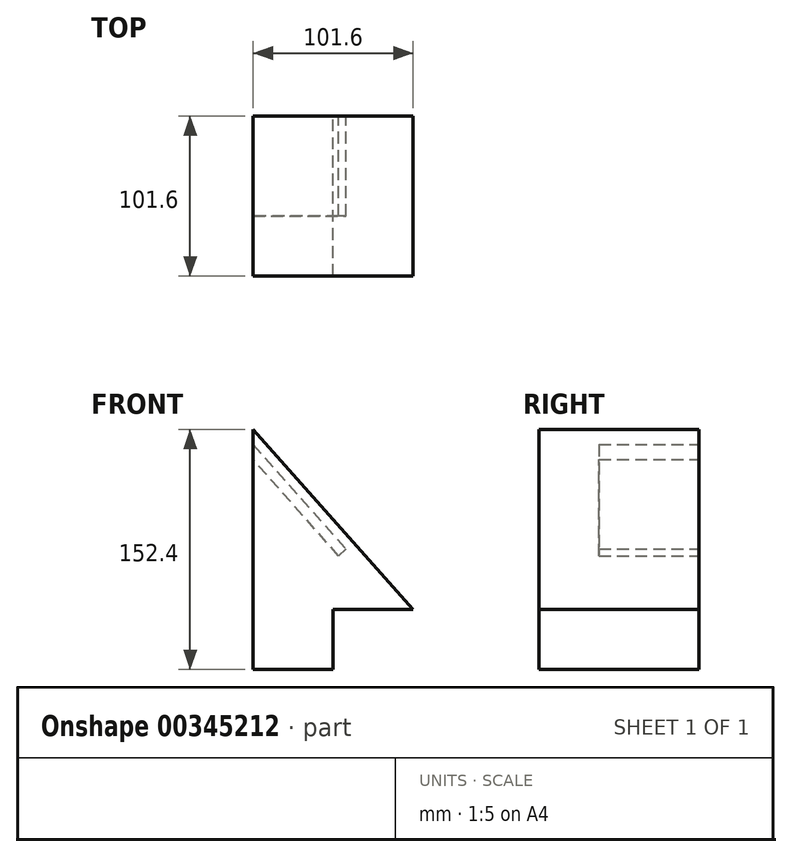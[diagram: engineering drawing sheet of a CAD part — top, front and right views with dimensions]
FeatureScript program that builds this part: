
annotation { "Feature Type Name" : "Feature", "Feature Type Description" : "" }
export const myFeature = defineFeature(function(context is Context, id is Id, definition is map)
    precondition{}
    {
        {
            var Q0;
            Q0=qCreatedBy(makeId("Front.planeOp"),FACE);
            var sketch = newSketch(context, id + "F0", { "sketchPlane" : qUnion([Q0])});
            skLineSegment(sketch, "E0.top", {"start": v(-61.33, -55.16) * mm, "end": v(-10.53, -55.16) * mm});
            skPoint(sketch, "E0.middle", {"position": v(-10.53, -36.1) * mm});
            skLineSegment(sketch, "E1", {"start": v(-10.53, -55.16) * mm, "end": v(-10.53, -17.06) * mm});
            skLineSegment(sketch, "E2", {"start": v(-10.53, -17.06) * mm, "end": v(40.27, -17.06) * mm});
            skLineSegment(sketch, "E3", {"start": v(40.27, -17.06) * mm, "end": v(-61.33, 97.24) * mm});
            skPoint(sketch, "E4.orphan", {"position": v(40.27, -55.16) * mm});
            skLineSegment(sketch, "E5", {"start": v(40.27, -17.06) * mm, "end": v(40.27, -17.06) * mm});
            skPoint(sketch, "E6.start.orphan", {"position": v(-61.33, -17.06) * mm});
            skLineSegment(sketch, "E7", {"start": v(-61.33, 97.24) * mm, "end": v(-61.33, -55.16) * mm});
            skSolve(sketch);
        }
        {
            var Q0;
            Q0=makeQuery(id+"F0.imprint","IMPRINT",FACE,{"disambiguationData":[TD([[makeQuery(id+"F0.imprint","IMPRINT",EDGE,{"derivedFrom":sQuery(id+"F0.wireOp",EDGE,"E0.top")}),1.0]])]});
            extrude(context, id + "F1", {"entities" : qUnion([Q0]), "depth" : 101.6 * mm});
        }
        {
            var Q0;
            Q0=makeQuery(id+"F1.opExtrude","CAP_FACE",FACE,{"disambiguationData":[OSD([sQuery(id+"F0.wireOp",EDGE,"E0.top"),sQuery(id+"F0.wireOp",EDGE,"E1"),sQuery(id+"F0.wireOp",EDGE,"E2"),sQuery(id+"F0.wireOp",EDGE,"E3"),sQuery(id+"F0.wireOp",EDGE,"E5"),sQuery(id+"F0.wireOp",EDGE,"E7")])],"isStart":true});
            var sketch = newSketch(context, id + "F2", { "sketchPlane" : qUnion([Q0])});
            skLineSegment(sketch, "E8", {"start": v(61.33, 87.68) * mm, "end": v(2.27, 21.24) * mm});
            skLineSegment(sketch, "E9", {"start": v(2.27, 21.24) * mm, "end": v(7.01, 17.02) * mm});
            skLineSegment(sketch, "E10", {"start": v(7.01, 17.02) * mm, "end": v(61.33, 78.13) * mm});
            skSolve(sketch);
        }
        {
            var Q0;
            {var subQ0=sQuery(id+"F2.wireOp",EDGE,"E8");Q0=makeQuery(id+"F2.imprint","IMPRINT",FACE,{"disambiguationData":[TD([[makeQuery(id+"F2.imprint","IMPRINT",EDGE,{"derivedFrom":subQ0}),1.0]])]});}
            extrude(context, id + "F3", {"entities" : qUnion([Q0]), "operationType" : NewBodyOperationType.REMOVE, "oppositeDirection" : true, "depth" : 63.5 * mm});
        }
    });
